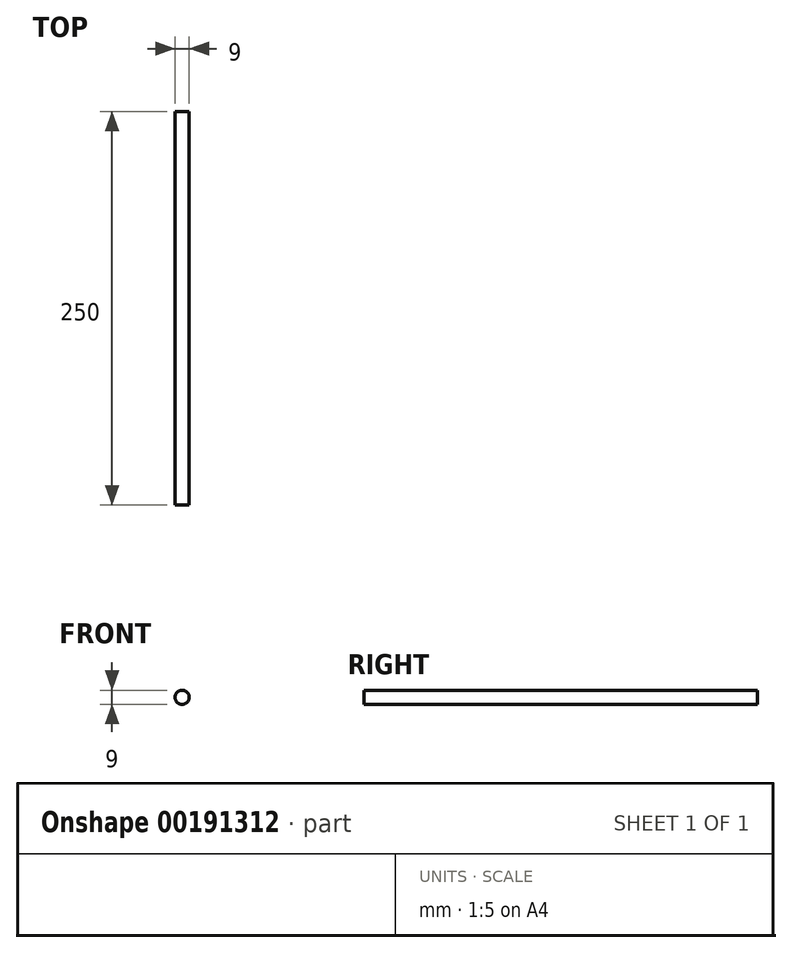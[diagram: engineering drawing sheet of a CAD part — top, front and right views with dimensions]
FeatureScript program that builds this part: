
annotation { "Feature Type Name" : "Feature", "Feature Type Description" : "" }
export const myFeature = defineFeature(function(context is Context, id is Id, definition is map)
    precondition{}
    {
        {
            var Q0;
            Q0=qCreatedBy(makeId("Front.planeOp"),FACE);
            var sketch = newSketch(context, id + "F0", { "sketchPlane" : qUnion([Q0])});
            skCircle(sketch, "E0", {"center": v(0, 0) * mm, "radius": 4.5 * mm});
            skSolve(sketch);
        }
        {
            var Q0;
            Q0 = qSketchRegion(id + "F0", true);
            extrude(context, id + "F1", {"entities" : qUnion([Q0]), "oppositeDirection" : true, "depth" : 250 * mm});
        }
    });
